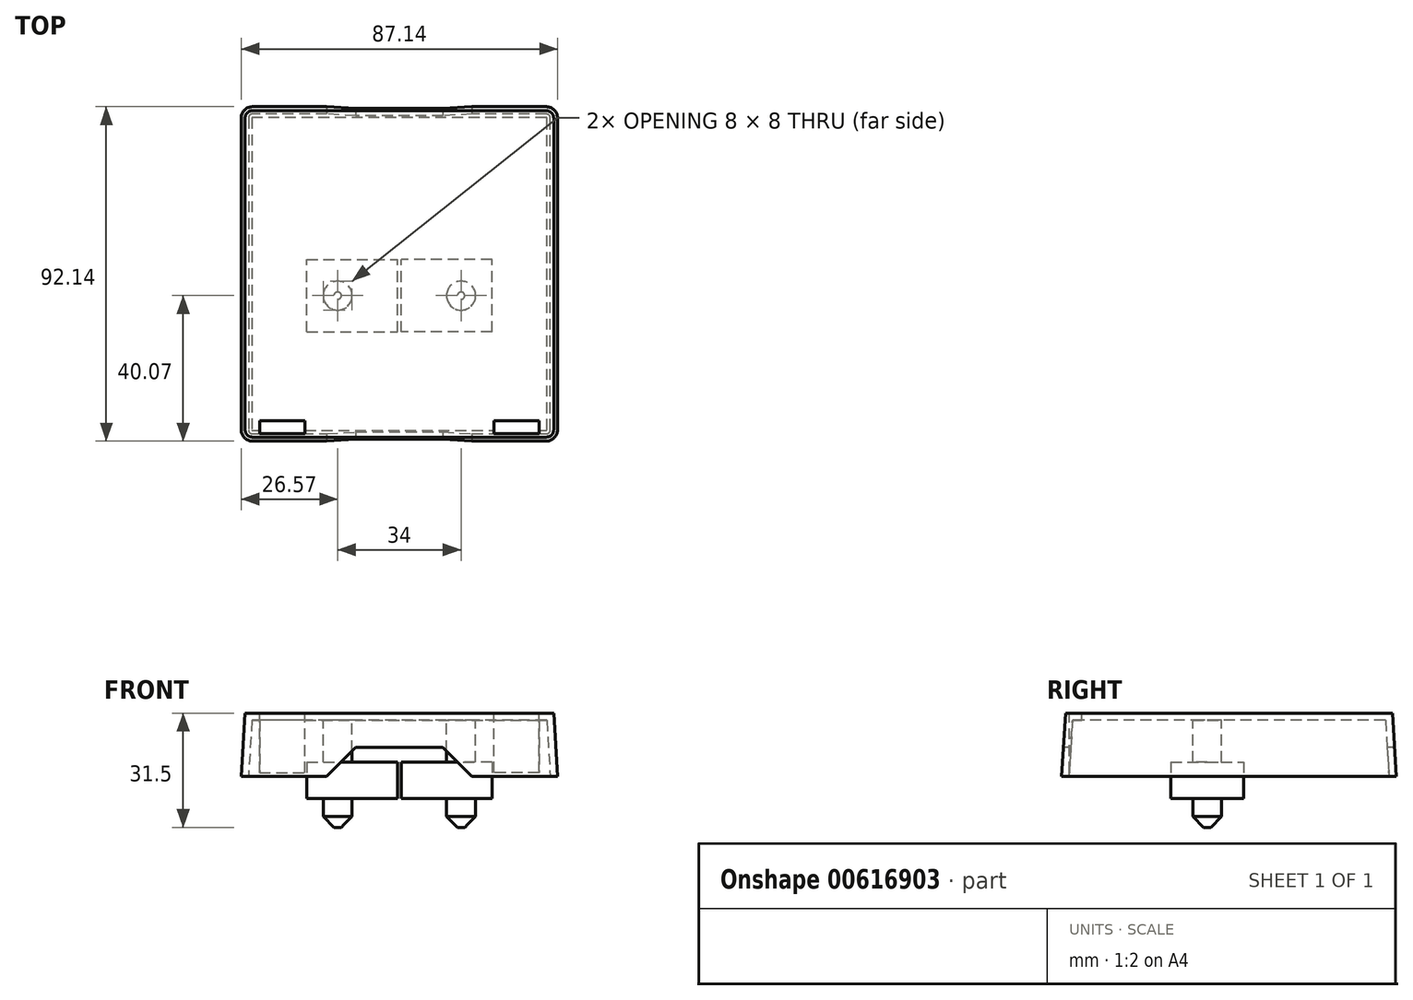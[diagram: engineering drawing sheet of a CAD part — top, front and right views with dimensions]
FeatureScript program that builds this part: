
annotation { "Feature Type Name" : "Feature", "Feature Type Description" : "" }
export const myFeature = defineFeature(function(context is Context, id is Id, definition is map)
    precondition{}
    {
        {
            var Q0;
            Q0=qCreatedBy(makeId("Top.planeOp"),FACE);
            var sketch = newSketch(context, id + "F0", { "sketchPlane" : qUnion([Q0])});
            skLineSegment(sketch, "E0.bottom", {"start": v(40.5, -45) * mm, "end": v(-40.5, -45) * mm});
            skLineSegment(sketch, "E0.top", {"start": v(40.5, 45) * mm, "end": v(-40.5, 45) * mm});
            skLineSegment(sketch, "E0.left", {"start": v(42.5, -43) * mm, "end": v(42.5, 43) * mm});
            skLineSegment(sketch, "E0.right", {"start": v(-42.5, -43) * mm, "end": v(-42.5, 43) * mm});
            skPoint(sketch, "E0.middle", {"position": v(0, 0) * mm});
            skPoint(sketch, "E1.visualSharp", {"position": v(-42.5, 45) * mm});
            skArc(sketch, "E1.filletArc", {"start": v(-40.5, 45) * mm, "mid": v(-41.91, 44.41) * mm, "end": v(-42.5, 43) * mm});
            skPoint(sketch, "E2.visualSharp", {"position": v(42.5, 45) * mm});
            skArc(sketch, "E2.filletArc", {"start": v(42.5, 43) * mm, "mid": v(41.91, 44.41) * mm, "end": v(40.5, 45) * mm});
            skPoint(sketch, "E3.visualSharp", {"position": v(42.5, -45) * mm});
            skArc(sketch, "E3.filletArc", {"start": v(40.5, -45) * mm, "mid": v(41.91, -44.41) * mm, "end": v(42.5, -43) * mm});
            skPoint(sketch, "E4.visualSharp", {"position": v(-42.5, -45) * mm});
            skArc(sketch, "E4.filletArc", {"start": v(-42.5, -43) * mm, "mid": v(-41.91, -44.41) * mm, "end": v(-40.5, -45) * mm});
            skSolve(sketch);
        }
        {
            var Q0;
            Q0 = qSketchRegion(id + "F0", true);
            extrude(context, id + "F1", {"entities" : qUnion([Q0]), "oppositeDirection" : true, "depth" : 17.5 * mm, "offsetDistance" : 25 * mm, "hasDraft" : true, "draftAngle" : 3.5 * degree});
        }
        {
            var Q0;
            Q0=qCreatedBy(makeId("Front.planeOp"),FACE);
            var sketch = newSketch(context, id + "F2", { "sketchPlane" : qUnion([Q0])});
            skLineSegment(sketch, "E5", {"start": v(0, 0) * mm, "end": v(0, -17.5) * mm, "construction": true});
            skLineSegment(sketch, "E6", {"start": v(0, -17.5) * mm, "end": v(-20, -17.5) * mm});
            skLineSegment(sketch, "E7", {"start": v(-20, -17.5) * mm, "end": v(-12, -9.5) * mm});
            skLineSegment(sketch, "E8", {"start": v(-12, -9.5) * mm, "end": v(0, -9.5) * mm});
            skLineSegment(sketch, "E9", {"start": v(0, -9.5) * mm, "end": v(12, -9.5) * mm});
            skLineSegment(sketch, "E10", {"start": v(12, -9.5) * mm, "end": v(20, -17.5) * mm});
            skLineSegment(sketch, "E11", {"start": v(20, -17.5) * mm, "end": v(0, -17.5) * mm});
            skSolve(sketch);
        }
        {
            var Q0;
            Q0 = qSketchRegion(id + "F2", true);
            extrude(context, id + "F3", {"entities" : qUnion([Q0]), "operationType" : NewBodyOperationType.REMOVE, "endBound" : BoundingType.SYMMETRIC, "oppositeDirection" : true, "depth" : 150 * mm, "offsetDistance" : 25 * mm});
        }
        {
            var Q0;
            {var subQ0=sQuery(id+"F0.wireOp",EDGE,"E1.filletArc");var subQ1=sQuery(id+"F0.wireOp",EDGE,"E0.top");var subQ2=sQuery(id+"F0.wireOp",EDGE,"E0.right");var subQ3=sQuery(id+"F0.wireOp",EDGE,"E0.bottom");var subQ4=sQuery(id+"F0.wireOp",EDGE,"E4.filletArc");Q0=makeQuery(id+"F3.boolean.opBoolean","SPLIT",FACE,{"disambiguationData":[TD([makeQuery(id+"F1.opExtrude","SWEPT_FACE",FACE,{"disambiguationData":[OSD([subQ2])]})])],"derivedFrom":makeQuery(id+"F1.opExtrude","CAP_FACE",FACE,{"disambiguationData":[OSD([subQ3,subQ1,sQuery(id+"F0.wireOp",EDGE,"E0.left"),subQ2,subQ0,sQuery(id+"F0.wireOp",EDGE,"E2.filletArc"),sQuery(id+"F0.wireOp",EDGE,"E3.filletArc"),subQ4])],"isStart":false})});}
            var Q1;
            Q1=makeQuery(id+"F3.boolean.opBoolean","COPY",FACE,{"derivedFrom":makeQuery(id+"F3.opExtrude","SWEPT_FACE",FACE,{"disambiguationData":[OSD([sQuery(id+"F2.wireOp",EDGE,"E7")])]})});
            var Q2;
            Q2=makeQuery(id+"F3.boolean.opBoolean","COPY",FACE,{"derivedFrom":makeQuery(id+"F3.opExtrude","SWEPT_FACE",FACE,{"disambiguationData":[OSD([sQuery(id+"F2.wireOp",EDGE,"E8"),sQuery(id+"F2.wireOp",EDGE,"E9")])]})});
            var Q3;
            Q3=makeQuery(id+"F3.boolean.opBoolean","COPY",FACE,{"derivedFrom":makeQuery(id+"F3.opExtrude","SWEPT_FACE",FACE,{"disambiguationData":[OSD([sQuery(id+"F2.wireOp",EDGE,"E10")])]})});
            var Q4;
            {var subQ0=sQuery(id+"F0.wireOp",EDGE,"E2.filletArc");var subQ1=sQuery(id+"F0.wireOp",EDGE,"E0.left");var subQ2=sQuery(id+"F0.wireOp",EDGE,"E0.top");var subQ3=sQuery(id+"F0.wireOp",EDGE,"E0.bottom");var subQ4=sQuery(id+"F0.wireOp",EDGE,"E3.filletArc");Q4=makeQuery(id+"F3.boolean.opBoolean","SPLIT",FACE,{"disambiguationData":[TD([makeQuery(id+"F1.opExtrude","SWEPT_FACE",FACE,{"disambiguationData":[OSD([subQ1])]})])],"derivedFrom":makeQuery(id+"F1.opExtrude","CAP_FACE",FACE,{"disambiguationData":[OSD([subQ3,subQ2,subQ1,sQuery(id+"F0.wireOp",EDGE,"E0.right"),sQuery(id+"F0.wireOp",EDGE,"E1.filletArc"),subQ0,subQ4,sQuery(id+"F0.wireOp",EDGE,"E4.filletArc")])],"isStart":false})});}
            shell(context, id + "F4", {"entities" : qUnion([Q0, Q1, Q2, Q3, Q4]), "thickness" : 2 * mm});
        }
        {
            var Q0;
            Q0=qCreatedBy(makeId("Top.planeOp"),FACE);
            var sketch = newSketch(context, id + "F5", { "sketchPlane" : qUnion([Q0])});
            skLineSegment(sketch, "E12", {"start": v(0, 0) * mm, "end": v(0, -44) * mm, "construction": true});
            skLineSegment(sketch, "E13", {"start": v(0, -44) * mm, "end": v(-26, -44) * mm, "construction": true});
            skLineSegment(sketch, "E14", {"start": v(-26, -44) * mm, "end": v(-26, -40.5) * mm});
            skLineSegment(sketch, "E15", {"start": v(-26, -40.5) * mm, "end": v(-38.5, -40.5) * mm});
            skLineSegment(sketch, "E16", {"start": v(-38.5, -40.5) * mm, "end": v(-38.5, -44) * mm});
            skLineSegment(sketch, "E17", {"start": v(-38.5, -44) * mm, "end": v(-26, -44) * mm});
            skLineSegment(sketch, "E18.MirrorCS", {"start": v(26, -44) * mm, "end": v(26, -40.5) * mm});
            skLineSegment(sketch, "E19.MirrorCS", {"start": v(26, -40.5) * mm, "end": v(38.5, -40.5) * mm});
            skLineSegment(sketch, "E20.MirrorCS", {"start": v(38.5, -40.5) * mm, "end": v(38.5, -44) * mm});
            skLineSegment(sketch, "E21.MirrorCS", {"start": v(38.5, -44) * mm, "end": v(26, -44) * mm});
            skSolve(sketch);
        }
        {
            var Q0;
            Q0 = qSketchRegion(id + "F5", true);
            extrude(context, id + "F6", {"entities" : qUnion([Q0]), "operationType" : NewBodyOperationType.REMOVE, "endBound" : BoundingType.THROUGH_ALL, "oppositeDirection" : true, "depth" : 25 * mm, "offsetDistance" : 25 * mm});
        }
        {
            var Q0;
            Q0=qCreatedBy(makeId("Top.planeOp"),FACE);
            var sketch = newSketch(context, id + "F7", { "sketchPlane" : qUnion([Q0])});
            skLineSegment(sketch, "E22", {"start": v(-17, -6) * mm, "end": v(17, -6) * mm, "construction": true});
            skLineSegment(sketch, "E23", {"start": v(0, 0) * mm, "end": v(0, -6) * mm, "construction": true});
            skCircle(sketch, "E24", {"center": v(-17, -6) * mm, "radius": 4 * mm});
            skCircle(sketch, "E25", {"center": v(17, -6) * mm, "radius": 4 * mm});
            skSolve(sketch);
        }
        {
            var Q0;
            Q0 = qSketchRegion(id + "F7", true);
            extrude(context, id + "F8", {"entities" : qUnion([Q0]), "operationType" : NewBodyOperationType.ADD, "oppositeDirection" : true, "depth" : 31.5 * mm, "offsetDistance" : 25 * mm});
        }
        {
            var Q0;
            Q0=makeQuery(id+"F8.opExtrude","CAP_EDGE",EDGE,{"disambiguationData":[OSD([sQuery(id+"F7.wireOp",EDGE,"E24")])],"isStart":false});
            var Q1;
            Q1=makeQuery(id+"F8.opExtrude","CAP_EDGE",EDGE,{"disambiguationData":[OSD([sQuery(id+"F7.wireOp",EDGE,"E25")])],"isStart":false});
            chamfer(context, id + "F9", {"entities" : qUnion([Q0, Q1]), "width" : 3 * mm, "tangentPropagation" : true});
        }
        {
            var Q0;
            Q0=makeQuery(id+"F8.opExtrude","CAP_FACE",FACE,{"disambiguationData":[OSD([sQuery(id+"F7.wireOp",EDGE,"E24")])],"isStart":false});
            cPlane(context, id + "F10", {"entities" : qUnion([Q0]), "cplaneType" : CPlaneType.OFFSET, "offset" : 8 * mm, "oppositeDirection" : true, "width" : 150 * mm, "height" : 150 * mm});
        }
        {
            var Q0;
            Q0=qCreatedBy(id+"F10.planeOp",FACE);
            var sketch = newSketch(context, id + "F11", { "sketchPlane" : qUnion([Q0])});
            skLineSegment(sketch, "E26", {"start": v(-17, 6) * mm, "end": v(17, 6) * mm, "construction": true});
            skLineSegment(sketch, "E27", {"start": v(0, 6) * mm, "end": v(0, 0) * mm, "construction": true});
            skLineSegment(sketch, "E28.bottom", {"start": v(-25.5, 16) * mm, "end": v(-0.5, 16) * mm});
            skLineSegment(sketch, "E28.top", {"start": v(-25.5, -4) * mm, "end": v(-0.5, -4) * mm});
            skLineSegment(sketch, "E28.left", {"start": v(-25.5, 16) * mm, "end": v(-25.5, -4) * mm});
            skLineSegment(sketch, "E28.right", {"start": v(-0.5, 16) * mm, "end": v(-0.5, -4) * mm});
            skPoint(sketch, "E28.middle", {"position": v(-13, 6) * mm});
            skLineSegment(sketch, "E29.MirrorCS", {"start": v(0.5, 16) * mm, "end": v(0.5, -4) * mm});
            skLineSegment(sketch, "E30.MirrorCS", {"start": v(25.5, 16) * mm, "end": v(0.5, 16) * mm});
            skLineSegment(sketch, "E31.MirrorCS", {"start": v(25.5, 16) * mm, "end": v(25.5, -4) * mm});
            skLineSegment(sketch, "E32.MirrorCS", {"start": v(25.5, -4) * mm, "end": v(0.5, -4) * mm});
            skSolve(sketch);
        }
        {
            var Q0;
            Q0 = qSketchRegion(id + "F11", true);
            extrude(context, id + "F12", {"entities" : qUnion([Q0]), "operationType" : NewBodyOperationType.ADD, "oppositeDirection" : true, "depth" : 10 * mm, "offsetDistance" : 25 * mm});
        }
    });
